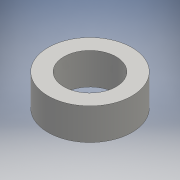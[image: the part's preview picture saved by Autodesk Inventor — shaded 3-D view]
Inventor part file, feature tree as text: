
AUTODESK INVENTOR PART (.ipt)
format: ipt  version: 2016 (Build 200138000, 138)  size: 91,648 bytes
history: native  units: mm
features: extrude x1, sketch x1
ambient origin geometry x8: Origin, YZ Plane, XZ Plane, XY Plane, X Axis, Y Axis, Z Axis, Center Point
bodies: Solid1 (feature_tree)
feature tree (2):
  extrude  "Extrusion1"  Depth=2.0mm
  sketch  "Sketch1"  dims[d0=3.3mm d1=1.0mm d2=2.0mm d3=0.0mm]
